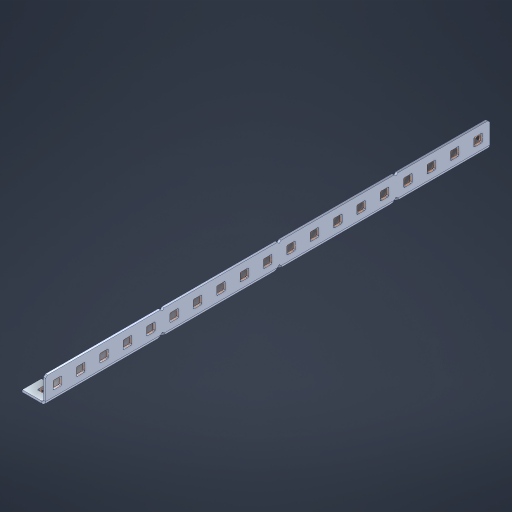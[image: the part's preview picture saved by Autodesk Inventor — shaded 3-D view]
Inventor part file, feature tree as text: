
AUTODESK INVENTOR PART (.ipt)
format: ipt  version: 2023 (Build 270158000, 158)  size: 912,384 bytes
history: native  units: in
note: dims shown in document units (in); Inventor stores cm internally (conversion verified against a paired STEP export)
features: other x64, extrude x55, sheet_metal_op x11, sketch x10, pattern_linear x2, mirror x1, chamfer x1
ambient origin geometry x8: Origin, YZ Plane, XZ Plane, XY Plane, X Axis, Y Axis, Z Axis, Center Point
bodies: Solid1 (feature_tree), Body (feature_tree)
feature tree (144):
  sheet_metal_op  "Flanges"
  other  "Flange Pattern Plane"
  other  "Flange Pattern Sketch"
  sheet_metal_op  "Flange Pattern"
  sheet_metal_op  "Body Pattern"
  pattern_linear  "Center Pattern"  Spacing1=0.0469in  [1 undecoded]
  other  "Arc Length"
  mirror  "Notch Mirror"
  pattern_linear  "Notch Pattern"  Spacing1=0.182in  [1 undecoded]
  chamfer  "End Chamfer"
  extrude  "Half Cut"  Depth=0.02in
  sketch  "Sketch1"  dims[d0=1.0in]
  other  "Plate1"
  sketch  "Sketch2"  dims[d1=9.5in]
  other  "Plate2"
  sheet_metal_op  "Bend1"
  sheet_metal_op  "Corner1"
  sketch  "Sketch3"  dims[d2=0.0469in]
  sketch  "Sketch7"  dims[d3=0.0469in]
  other  "Srf1"
  other  "Srf2"
  sketch  "Sketch8"  dims[d4=0.0234in]
  sketch  "Sketch9"  dims[d5=0.0938in]
  other  "Srf91"
  sheet_metal_op  "Body Pattern Sketch"
  other  "Srf92"
  sketch  "Sketch13"  dims[d6=0.0469in]
  sketch  "Sketch14"  dims[d7=0.5in d8=90.0deg d9=0.0312in]
  sketch  "Sketch15"  dims[d10=0.1875in]
  sketch  "Sketch16"  dims[d11=0.0469in d12=0.0469in d16=0.182in d17=0.02in d18=0.0469in d19=0.0in d20=0.25in d21=0.25in d38=7.4803in d40=0.5in d41=0.3937in d43=1.0in d46=0.172in d47=1.0in d48=0.0in d49=0.182in d50=0.02in d51=0.25in d52=0.25in d53=0.0469in d54=0.0in d55=0.172in d56=1.0in d57=0.0in d58=0.25in d60=7.4803in d62=0.5in d63=0.3937in d65=0.5in d85=0.1227in d86=0.1659in d88=0.04in d89=0.0469in d90=0.0in d91=0.04in d92=0.0491in d95=2.5in d96=0.04in d97=0.25in d98=45.0deg d99=0.25in d100=0.5in d101=0.0in d102=2.497in d106=0.182in d107=0.02in d108=0.5in d109=0.5in d110=0.0469in d111=0.0in d112=0.172in d113=0.5in d114=0.0in d117=0.5in d118=0.5in d119=0.5in]
  other  "Srf786"
  other  "Srf823"
  other  "Srf824"
  other  "Srf825"
  other  "Srf826"
  other  "Srf827"
  other  "Srf828"
  other  "Srf829"
  other  "Srf856"
  other  "Srf857"
  other  "Srf858"
  other  "Srf859"
  other  "Srf860"
  other  "Srf861"
  other  "Srf862"
  other  "Srf889"
  other  "Srf890"
  other  "Srf891"
  other  "Srf892"
  other  "Srf893"
  other  "Srf894"
  other  "Srf895"
  other  "Srf896"
  other  "Srf922"
  other  "Srf923"
  other  "Srf924"
  other  "Srf925"
  other  "Srf926"
  other  "Srf959"
  other  "Srf960"
  other  "Srf961"
  other  "Srf962"
  other  "Srf963"
  other  "Srf996"
  other  "Srf997"
  other  "Srf998"
  other  "Srf999"
  other  "Srf1000"
  other  "Srf1143"
  other  "Srf1144"
  other  "Srf1145"
  other  "Srf1146"
  other  "Srf1147"
  other  "Srf1199"
  other  "Srf1200"
  other  "Srf1201"
  other  "Srf1202"
  other  "Srf1203"
  other  "Srf1255"
  other  "Srf1256"
  other  "Srf1257"
  other  "Srf1258"
  other  "Srf1259"
  sheet_metal_op  "Flange Stamp"
  sheet_metal_op  "Flange Circle"
  sheet_metal_op  "Body Stamp"
  sheet_metal_op  "Body Circle"
  other  "Center Stamp"
  other  "Center Circle"
  sheet_metal_op  "Notch"
  extrude  "ExtrusionSrf2"  Depth=0.0469in
  extrude  "ExtrusionSrf92"  TaperAngle=0.0deg  [1 undecoded]
  extrude  "ExtrusionSrf823"  Depth=0.5in
  extrude  "ExtrusionSrf824"  Depth=0.5in
  extrude  "ExtrusionSrf825"  Depth=0.5in
  extrude  "ExtrusionSrf826"  Depth=0.5in
  extrude  "ExtrusionSrf827"  Depth=1.0in TaperAngle=0.0deg
  extrude  "ExtrusionSrf828"  Depth=0.182in
  extrude  "ExtrusionSrf829"  Depth=0.02in
  extrude  "ExtrusionSrf856"  Depth=0.5in
  extrude  "ExtrusionSrf857"  Depth=0.5in
  extrude  "ExtrusionSrf858"  Depth=0.0469in
  extrude  "ExtrusionSrf859"  TaperAngle=0.0deg  [1 undecoded]
  extrude  "ExtrusionSrf860"  Depth=0.5in
  extrude  "ExtrusionSrf861"  Depth=1.0in TaperAngle=0.0deg
  extrude  "ExtrusionSrf862"  Depth=0.5in
  extrude  "ExtrusionSrf889"  Depth=0.5in
  extrude  "ExtrusionSrf890"  Depth=0.5in
  extrude  "ExtrusionSrf891"  Depth=0.5in
  extrude  "ExtrusionSrf892"  Depth=0.5in
  extrude  "ExtrusionSrf893"  Depth=0.5in
  extrude  "ExtrusionSrf894"  Depth=0.0469in
  extrude  "ExtrusionSrf895"  TaperAngle=0.0deg  [1 undecoded]
  extrude  "ExtrusionSrf896"  Depth=0.5in
  extrude  "ExtrusionSrf922"  Depth=0.5in
  extrude  "ExtrusionSrf923"  Depth=0.5in
  extrude  "ExtrusionSrf924"  Depth=0.5in TaperAngle=45.0deg
  extrude  "ExtrusionSrf925"  Depth=0.5in
  extrude  "ExtrusionSrf926"  Depth=0.5in TaperAngle=0.0deg
  extrude  "ExtrusionSrf959"  Depth=0.5in
  extrude  "ExtrusionSrf960"  Depth=0.182in
  extrude  "ExtrusionSrf961"  Depth=0.02in
  extrude  "ExtrusionSrf962"  Depth=0.5in
  extrude  "ExtrusionSrf963"  Depth=0.5in
  extrude  "ExtrusionSrf996"  Depth=0.0469in
  extrude  "ExtrusionSrf997"  TaperAngle=0.0deg  [1 undecoded]
  extrude  "ExtrusionSrf998"  Depth=0.5in
  extrude  "ExtrusionSrf999"  Depth=0.5in TaperAngle=0.0deg
  extrude  "ExtrusionSrf1000"  Depth=0.5in
  extrude  "ExtrusionSrf1143"  Depth=0.5in
  extrude  "ExtrusionSrf1144"  Depth=0.5in
  extrude  "ExtrusionSrf1145"  [1 undecoded]
  extrude  "ExtrusionSrf1146"  [1 undecoded]
  extrude  "ExtrusionSrf1147"  [1 undecoded]
  extrude  "ExtrusionSrf1199"  [1 undecoded]
  extrude  "ExtrusionSrf1200"  [1 undecoded]
  extrude  "ExtrusionSrf1201"  [1 undecoded]
  extrude  "ExtrusionSrf1202"  [1 undecoded]
  extrude  "ExtrusionSrf1203"  [1 undecoded]
  extrude  "ExtrusionSrf1255"  [1 undecoded]
  extrude  "ExtrusionSrf1256"  [1 undecoded]
  extrude  "ExtrusionSrf1257"  [1 undecoded]
  extrude  "ExtrusionSrf1258"  [1 undecoded]
  extrude  "ExtrusionSrf1259"  [1 undecoded]
note: 19 required parameter values undecoded (feature->parameter linkage not recoverable at this tier; creation-order binding heuristic only, values carry confidence <= 0.55)
